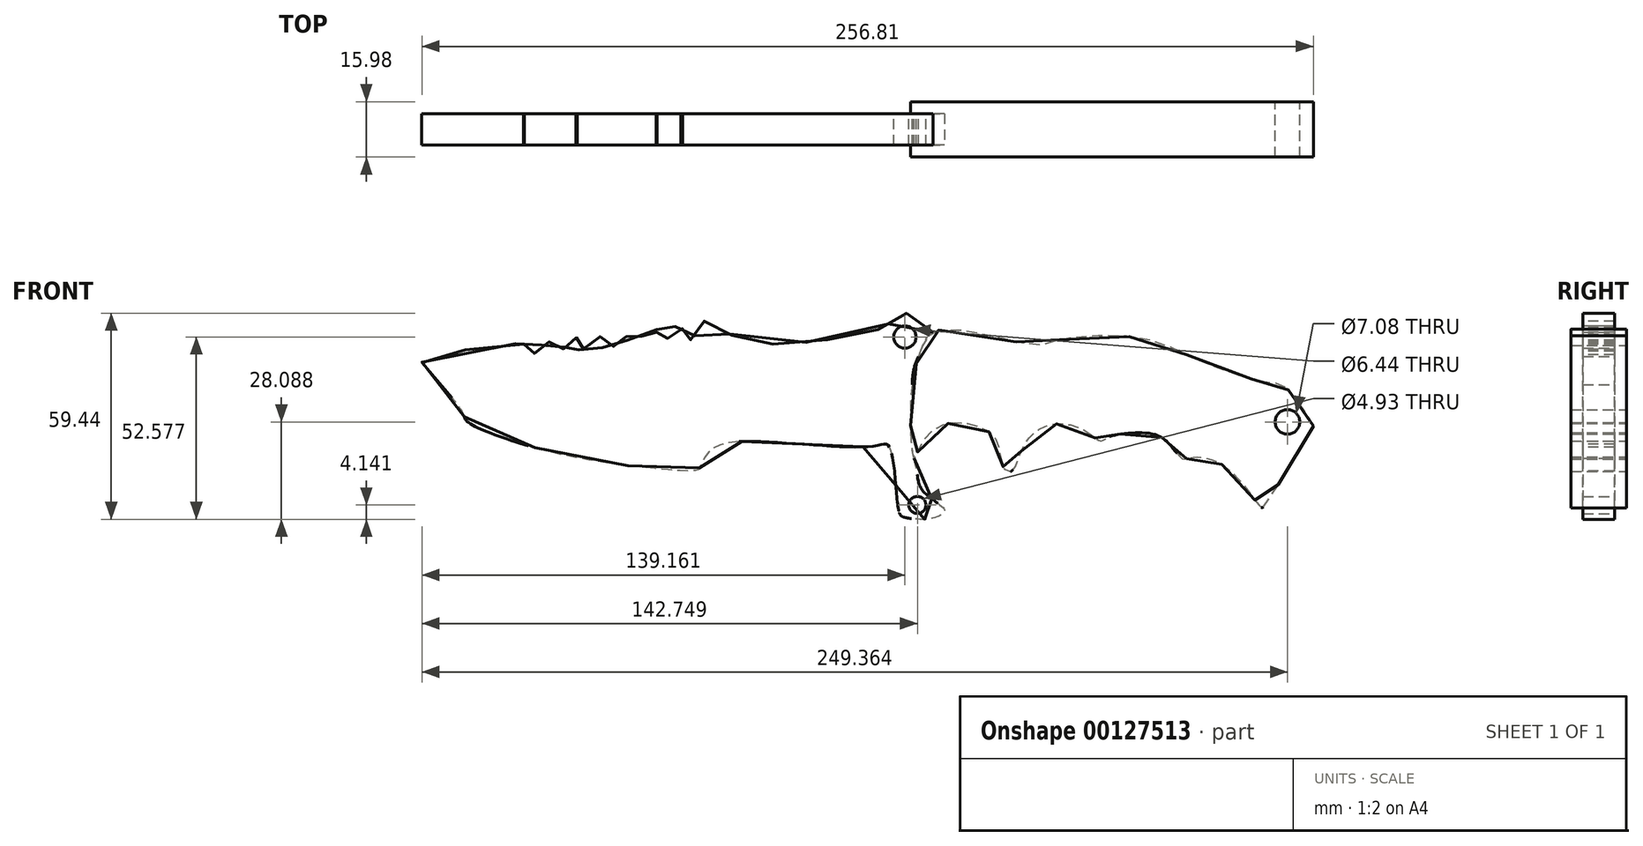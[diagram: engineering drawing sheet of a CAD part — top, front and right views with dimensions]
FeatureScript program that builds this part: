
annotation { "Feature Type Name" : "Feature", "Feature Type Description" : "" }
export const myFeature = defineFeature(function(context is Context, id is Id, definition is map)
    precondition{}
    {
        {
            var Q0;
            Q0=qCreatedBy(makeId("Front.planeOp"),FACE);
            var sketch = newSketch(context, id + "F0", { "sketchPlane" : qUnion([Q0])});
            skFitSpline(sketch, "E0", {"points": [v(81.36, 18.89) * mm, v(75.92, 12.58) * mm, v(73.3, 0) * mm, v(74.18, -18.1) * mm, v(76.14, -14.19) * mm, v(83.32, -8.1) * mm, v(92.9, -8.96) * mm, v(98.11, -13.32) * mm, v(100.07, -20.93) * mm, v(102.47, -21.58) * mm, v(106.16, -13.75) * mm, v(115.09, -8.1) * mm, v(124.44, -10.7) * mm, v(127.93, -13.1) * mm, v(130.1, -12.01) * mm, v(138.37, -10.7) * mm, v(146.42, -12.66) * mm, v(151.43, -18.1) * mm, v(153.6, -17.89) * mm, v(160.35, -18.54) * mm, v(169.05, -25.72) * mm, v(174.28, -32.25) * mm, v(175.15, -31.6) * mm, v(188.86, -9.83) * mm, v(188.64, -7.44) * mm, v(181.02, 2.57) * mm, v(176.45, 3.66) * mm, v(155.78, 10.4) * mm, v(138.8, 16.71) * mm, v(115.09, 15.84) * mm, v(109.43, 14.54) * mm, v(81.36, 18.89) * mm]});
            skCircle(sketch, "E1", {"center": v(181.75, -7.56) * mm, "radius": 3.54 * mm});
            skLineSegment(sketch, "E2", {"start": v(82.62, 4.3) * mm, "end": v(170.65, -8.1) * mm, "construction": true});
            skSolve(sketch);
        }
        {
            var Q0;
            Q0=makeQuery(id+"F0.imprint","IMPRINT",FACE,{"disambiguationData":[TD([[makeQuery(id+"F0.imprint","IMPRINT",EDGE,{"derivedFrom":sQuery(id+"F0.wireOp",EDGE,"E0")}),1.0]])]});
            extrude(context, id + "F1", {"entities" : qUnion([Q0]), "endBound" : BoundingType.SYMMETRIC, "depth" : 15.97 * mm});
        }
        {
            var Q0;
            Q0=qCreatedBy(makeId("Front.planeOp"),FACE);
            var sketch = newSketch(context, id + "F2", { "sketchPlane" : qUnion([Q0])});
            skFitSpline(sketch, "E3", {"points": [v(79.6, 18.28) * mm, v(75.8, 11.82) * mm, v(73.52, 0) * mm, v(74.09, -17.8) * mm, v(75.04, -22.35) * mm, v(76.75, -27.47) * mm, v(82.82, -32.6) * mm, v(82.63, -33.74) * mm, v(79.02, -35.45) * mm, v(71.43, -35.07) * mm, v(69.72, -32.98) * mm, v(67.06, -14.75) * mm, v(62.13, -14.56) * mm, v(23.97, -13.24) * mm, v(14.67, -16.65) * mm, v(12.39, -20.83) * mm, v(11.25, -21.59) * mm, v(-10.4, -19.88) * mm, v(-34.5, -15.13) * mm, v(-54.63, -7.35) * mm, v(-56.14, -4.31) * mm, v(-67.34, 9.17) * mm, v(-66.59, 10.68) * mm, v(-38.3, 14.86) * mm, v(-38.3, 13.72) * mm, v(-36.02, 11.82) * mm, v(-32.41, 15.43) * mm, v(-31.08, 15.81) * mm, v(-30.14, 13.53) * mm, v(-26.9, 13.34) * mm, v(-25.58, 16.57) * mm, v(-22.92, 16.57) * mm, v(-23.11, 13.72) * mm, v(-20.45, 13.72) * mm, v(-16.47, 17.7) * mm, v(-15.9, 14.3) * mm, v(-12.67, 13.91) * mm, v(-9.44, 18.28) * mm, v(-8.3, 16) * mm, v(-6.03, 15.43) * mm, v(-2.42, 19.04) * mm, v(0, 19.23) * mm, v(0, 16) * mm, v(2.7, 16) * mm, v(5.55, 19.99) * mm, v(7.45, 19.23) * mm, v(7.07, 16.76) * mm, v(10.3, 16.38) * mm, v(12.58, 21.13) * mm, v(16.95, 20.18) * mm, v(26.25, 15.62) * mm, v(46.56, 15.81) * mm, v(66.11, 20.18) * mm, v(72.57, 23.78) * mm, v(79.6, 18.28) * mm]});
            skCircle(sketch, "E4", {"center": v(71.55, 16.93) * mm, "radius": 3.22 * mm});
            skCircle(sketch, "E5", {"center": v(75.14, -31.5) * mm, "radius": 2.47 * mm});
            skSolve(sketch);
        }
        {
            var Q0;
            Q0=makeQuery(id+"F2.imprint","IMPRINT",FACE,{"disambiguationData":[TD([[makeQuery(id+"F2.imprint","IMPRINT",EDGE,{"derivedFrom":sQuery(id+"F2.wireOp",EDGE,"E3")}),-1.0]])]});
            extrude(context, id + "F3", {"entities" : qUnion([Q0]), "operationType" : NewBodyOperationType.ADD, "endBound" : BoundingType.SYMMETRIC, "depth" : 9.12 * mm});
        }
    });
